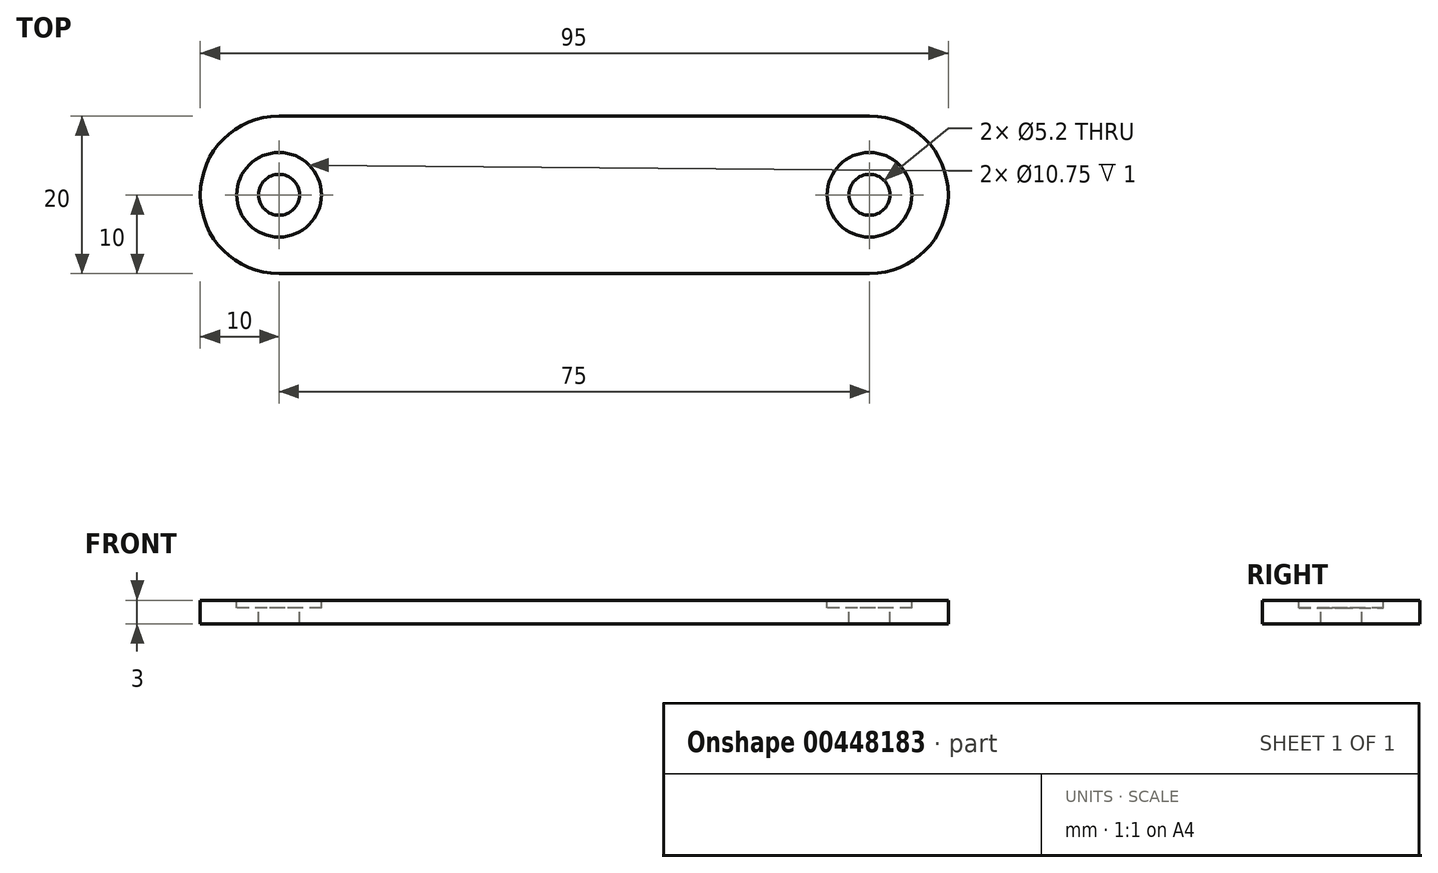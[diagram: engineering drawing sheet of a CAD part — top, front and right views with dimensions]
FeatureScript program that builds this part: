
annotation { "Feature Type Name" : "Feature", "Feature Type Description" : "" }
export const myFeature = defineFeature(function(context is Context, id is Id, definition is map)
    precondition{}
    {
        {
            var Q0;
            Q0=qCreatedBy(makeId("Top.planeOp"),FACE);
            var sketch = newSketch(context, id + "F0", { "sketchPlane" : qUnion([Q0])});
            skArc(sketch, "E0", {"start": v(0, 10) * mm, "mid": v(-10, 0) * mm, "end": v(0, -10) * mm});
            skArc(sketch, "E1", {"start": v(75, -10) * mm, "mid": v(85, 0) * mm, "end": v(75, 10) * mm});
            skLineSegment(sketch, "E2", {"start": v(0, 10) * mm, "end": v(75, 10) * mm});
            skLineSegment(sketch, "E3", {"start": v(0, -10) * mm, "end": v(75, -10) * mm});
            skCircle(sketch, "E4", {"center": v(0, 0) * mm, "radius": 5.38 * mm});
            skCircle(sketch, "E5", {"center": v(0, 0) * mm, "radius": 2.6 * mm});
            skCircle(sketch, "E6", {"center": v(75, 0) * mm, "radius": 5.38 * mm});
            skCircle(sketch, "E7", {"center": v(75, 0) * mm, "radius": 2.6 * mm});
            skSolve(sketch);
        }
        {
            var Q0;
            Q0=makeQuery(id+"F0.imprint","IMPRINT",FACE,{"disambiguationData":[TD([[makeQuery(id+"F0.imprint","IMPRINT",EDGE,{"derivedFrom":sQuery(id+"F0.wireOp",EDGE,"E0")}),1.0]])]});
            var Q1;
            Q1=makeQuery(id+"F0.imprint","IMPRINT",FACE,{"disambiguationData":[TD([[makeQuery(id+"F0.imprint","IMPRINT",EDGE,{"derivedFrom":sQuery(id+"F0.wireOp",EDGE,"E6")}),1.0]])]});
            var Q2;
            Q2=makeQuery(id+"F0.imprint","IMPRINT",FACE,{"disambiguationData":[TD([[makeQuery(id+"F0.imprint","IMPRINT",EDGE,{"derivedFrom":sQuery(id+"F0.wireOp",EDGE,"E4")}),1.0]])]});
            extrude(context, id + "F1", {"entities" : qUnion([Q0, Q1, Q2]), "oppositeDirection" : true, "depth" : 3 * mm});
        }
        {
            var Q0;
            Q0=makeQuery(id+"F0.imprint","IMPRINT",FACE,{"disambiguationData":[TD([[makeQuery(id+"F0.imprint","IMPRINT",EDGE,{"derivedFrom":sQuery(id+"F0.wireOp",EDGE,"E6")}),1.0]])]});
            var Q1;
            Q1=makeQuery(id+"F0.imprint","IMPRINT",FACE,{"disambiguationData":[TD([[makeQuery(id+"F0.imprint","IMPRINT",EDGE,{"derivedFrom":sQuery(id+"F0.wireOp",EDGE,"E4")}),1.0]])]});
            extrude(context, id + "F2", {"entities" : qUnion([Q0, Q1]), "operationType" : NewBodyOperationType.REMOVE, "oppositeDirection" : true, "depth" : 1 * mm});
        }
    });
